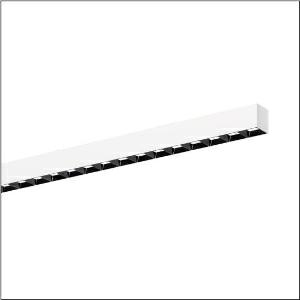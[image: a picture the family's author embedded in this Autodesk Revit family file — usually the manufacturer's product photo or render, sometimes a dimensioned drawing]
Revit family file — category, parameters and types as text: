
# Revit family: silica_r__21_51mx24da34wb_1271
name_source: partatom
category: Lighting Fixtures
units: mm (PartAtom-declared; Revit-internal decimal feet)

## family parameters
Cut with Voids When Loaded = No
Host = Face
Light Source = No
Part Type = Normal
Room Calculation Point = No
Round Connector Dimension = Use Diameter
Shared = No

## types (1)
- --- (1 x LED, 4320 lm, 32.1 W, 3000K)
    Apparent Load = 32 VA
    CIE Flux Codes = 74 94 99 100 100
    Color Rendering = 80
    Color Temperature = 3000K
    Default Elevation = 1800 mm
    Description = Silica® 21, office luminaire, primary light control with darklight reflector, of PMMA, black, CAT 2 (L<= 3000cd/m²), light emission: direct distribution, primary light characteristic: asymmetric, installation type: surface-mounted, LED, rated luminous flux: 4.320lm, luminous efficacy: 135lm/W, light colour: 830, colour temperature: 3000K, with terminal, 3+2-pole, max. 2.5mm², mains connection: 220..240V, AC, 50/60Hz, rated input power: 32.1W, luminaire housing, of aluminium, traffic white (RAL 9016), length: 1.204mm, width: 53mm, height: 53mm, protection rating (complete): IP20, insulation class (complete): insulation class I (protective earthing), certification: CE, permissible operating ambient temperature: 0..+35°C, standard: EN 50419, packaging unit: 1 piece
    Height = 0 mm  [stored 0 ft]
    Lamp = 1 x LED
    Lamp Light Flux = 4320 lm
    Lamp Power = 32.1 W
    Lamp count = 1
    Length = 1204 mm
    Luminous efficacy = 135 lm/W
    Manufacturer = Siteco
    ModVariant = No
    Model = 51MX24DA34WB
    Mounting Place = Ceiling
    Mounting Type = Recessed
    Number of Poles = 1
    OnlyDefault = Yes
    Power Factor = 1
    Product Name = Silica® 21
    Product group = office luminaire | ceiling recessed
    ProductGroupID = 401
    Protection Class = Protection class I
    Protection Degree = IP 20
    RLX_Detail_Level = 1
    RLX_Emergency_Light_Flux = 0 lm
    RLX_Emergency_Type = 0
    RLX_Emergency_Type_DB = No
    RlxData = <blob elided: 41913 chars, md5=4efcbe68>
    Socket = socket
    Standby Power = 0 W
    System Light Flux = 4320 lm
    System Power = 32 W
    Type Comments = factory setting: luminous flux: 100 % | dim-lin: 254 | 448 mA
    Type Image = l_1297779.jpg
    URL = http://relux.com
    VarID = @adj_053939
    Voltage = 0 V
    Weight = 0.00 kg
    Width = 53 mm

note: [stored X ft] marks values corroborated as IEEE doubles in the binary element streams (Revit-internal decimal feet)

## geometry (parser evidence)
native form markers: Blend x4, Sweep x10
no freeform markers — native parametric forms only
